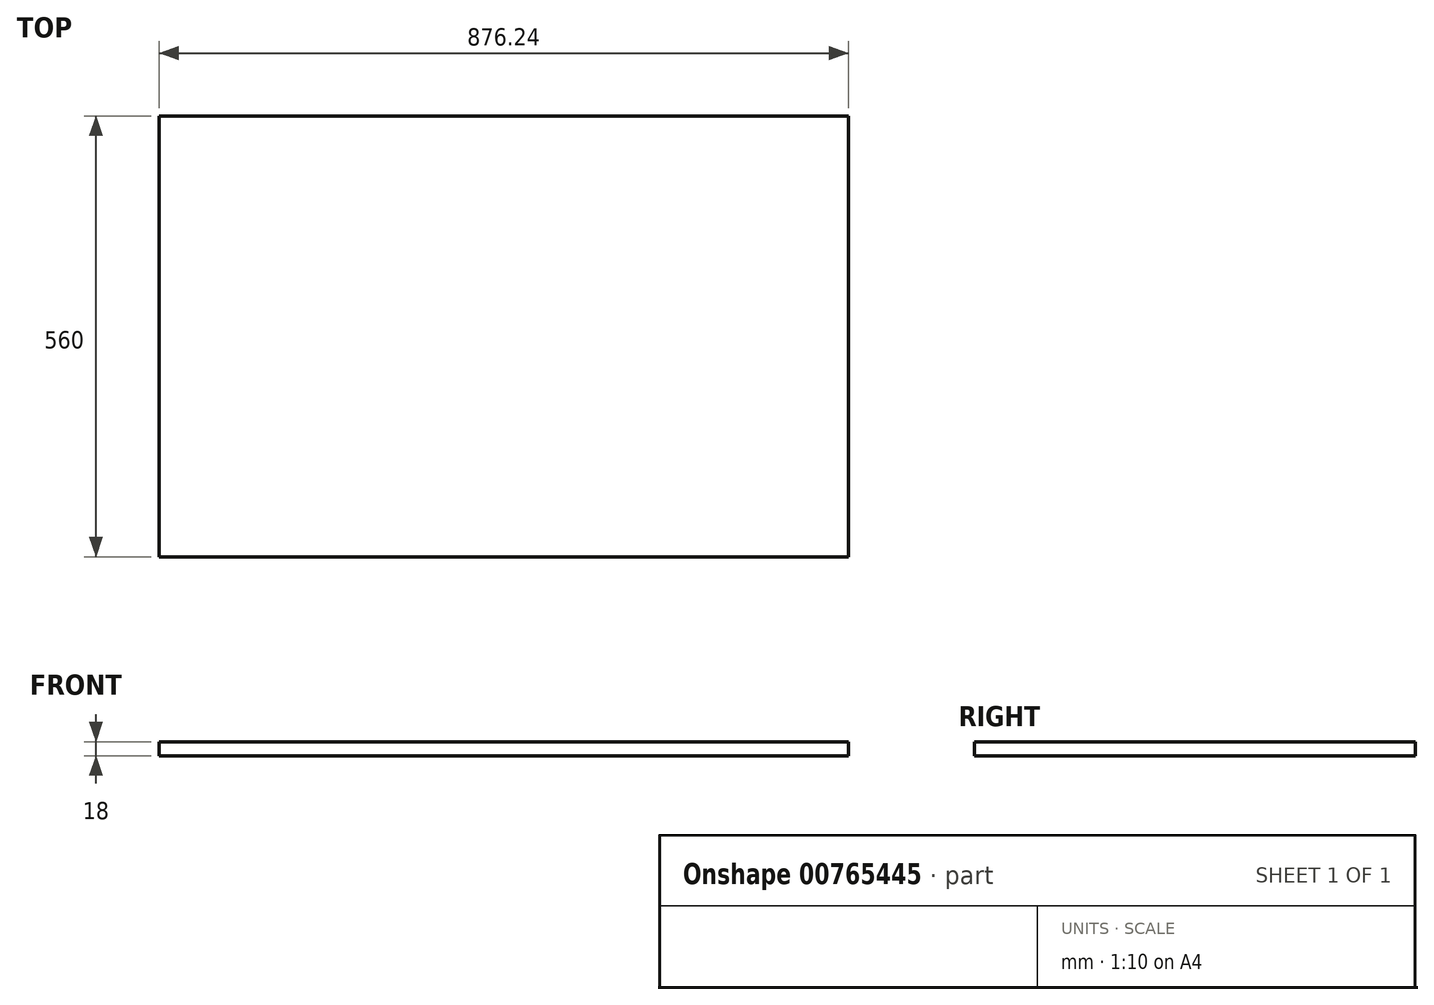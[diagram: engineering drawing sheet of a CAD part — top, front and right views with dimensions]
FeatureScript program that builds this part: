
annotation { "Feature Type Name" : "Feature", "Feature Type Description" : "" }
export const myFeature = defineFeature(function(context is Context, id is Id, definition is map)
    precondition{}
    {
        {
            var Q0;
            Q0=qCreatedBy(makeId("Top.planeOp"),FACE);
            var sketch = newSketch(context, id + "F0", { "sketchPlane" : qUnion([Q0])});
            skLineSegment(sketch, "E0.bottom", {"start": v(-438.12, -280) * mm, "end": v(438.13, -280) * mm});
            skLineSegment(sketch, "E0.top", {"start": v(-438.12, 280) * mm, "end": v(438.12, 280) * mm});
            skLineSegment(sketch, "E0.left", {"start": v(-438.12, -280) * mm, "end": v(-438.13, 280) * mm});
            skLineSegment(sketch, "E0.right", {"start": v(438.13, -280) * mm, "end": v(438.12, 280) * mm});
            skPoint(sketch, "E0.middle", {"position": v(0, 0) * mm});
            skSolve(sketch);
        }
        {
            var Q0;
            Q0 = qSketchRegion(id + "F0", true);
            extrude(context, id + "F1", {"entities" : qUnion([Q0]), "depth" : 18 * mm, "offsetDistance" : 25 * mm});
        }
    });
